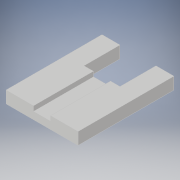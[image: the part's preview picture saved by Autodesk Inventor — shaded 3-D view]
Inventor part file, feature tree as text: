
AUTODESK INVENTOR PART (.ipt)
format: ipt  version: 2019 (Build 230136000, 136)  size: 120,320 bytes
history: native  units: in
note: dims shown in document units (in); Inventor stores cm internally (conversion verified against a paired STEP export)
features: extrude x2, sketch x2, projected_geometry x1
ambient origin geometry x8: Origin, YZ Plane, XZ Plane, XY Plane, X Axis, Y Axis, Z Axis, Center Point
bodies: Solid1 (feature_tree)
feature tree (5):
  extrude  "Extrusion1"  Depth=1.5748in
  extrude  "Extrusion2"  Depth=0.5906in
  sketch  "Sketch1"  dims[d2=1.1811in d3=1.5748in]
  sketch  "Sketch2"  dims[d4=0.5906in d5=0.5906in d6=0.1181in d7=0.0in d8=0.2805in d9=0.0787in d10=0.0in]
  projected_geometry  "Projected Loop1"
